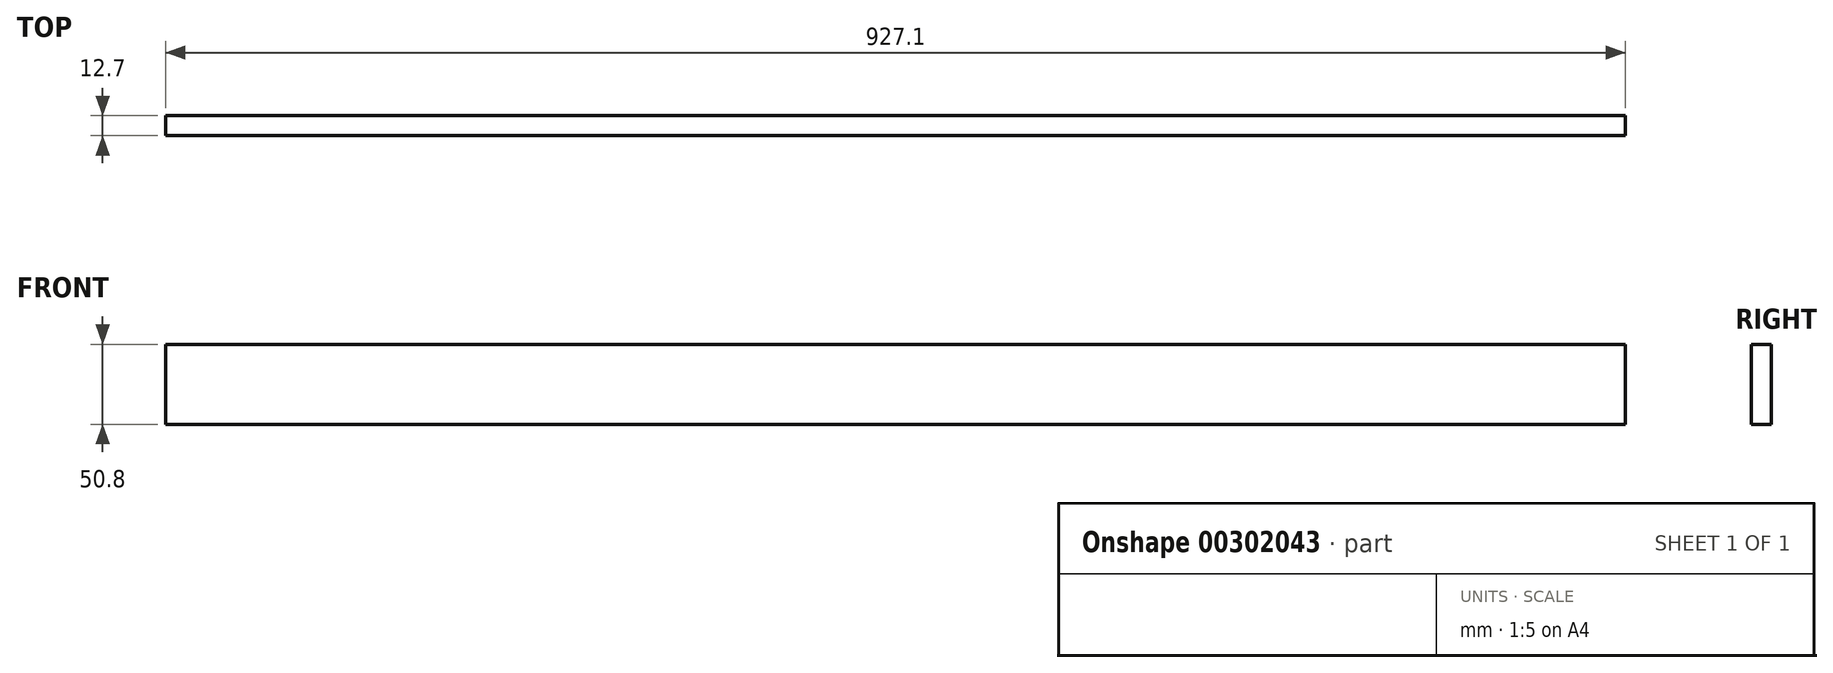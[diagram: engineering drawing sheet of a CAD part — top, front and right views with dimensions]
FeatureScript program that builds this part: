
annotation { "Feature Type Name" : "Feature", "Feature Type Description" : "" }
export const myFeature = defineFeature(function(context is Context, id is Id, definition is map)
    precondition{}
    {
        {
            var Q0;
            Q0=qCreatedBy(makeId("Top.planeOp"),FACE);
            var sketch = newSketch(context, id + "F0", { "sketchPlane" : qUnion([Q0])});
            skLineSegment(sketch, "E0.bottom", {"start": v(0, 0) * mm, "end": v(927.1, 0) * mm});
            skLineSegment(sketch, "E0.top", {"start": v(0, 12.7) * mm, "end": v(927.1, 12.7) * mm});
            skLineSegment(sketch, "E0.left", {"start": v(0, 0) * mm, "end": v(0, 12.7) * mm});
            skLineSegment(sketch, "E0.right", {"start": v(927.1, 0) * mm, "end": v(927.1, 12.7) * mm});
            skSolve(sketch);
        }
        {
            var Q0;
            Q0 = qSketchRegion(id + "F0", true);
            extrude(context, id + "F1", {"entities" : qUnion([Q0]), "depth" : 50.8 * mm});
        }
    });
